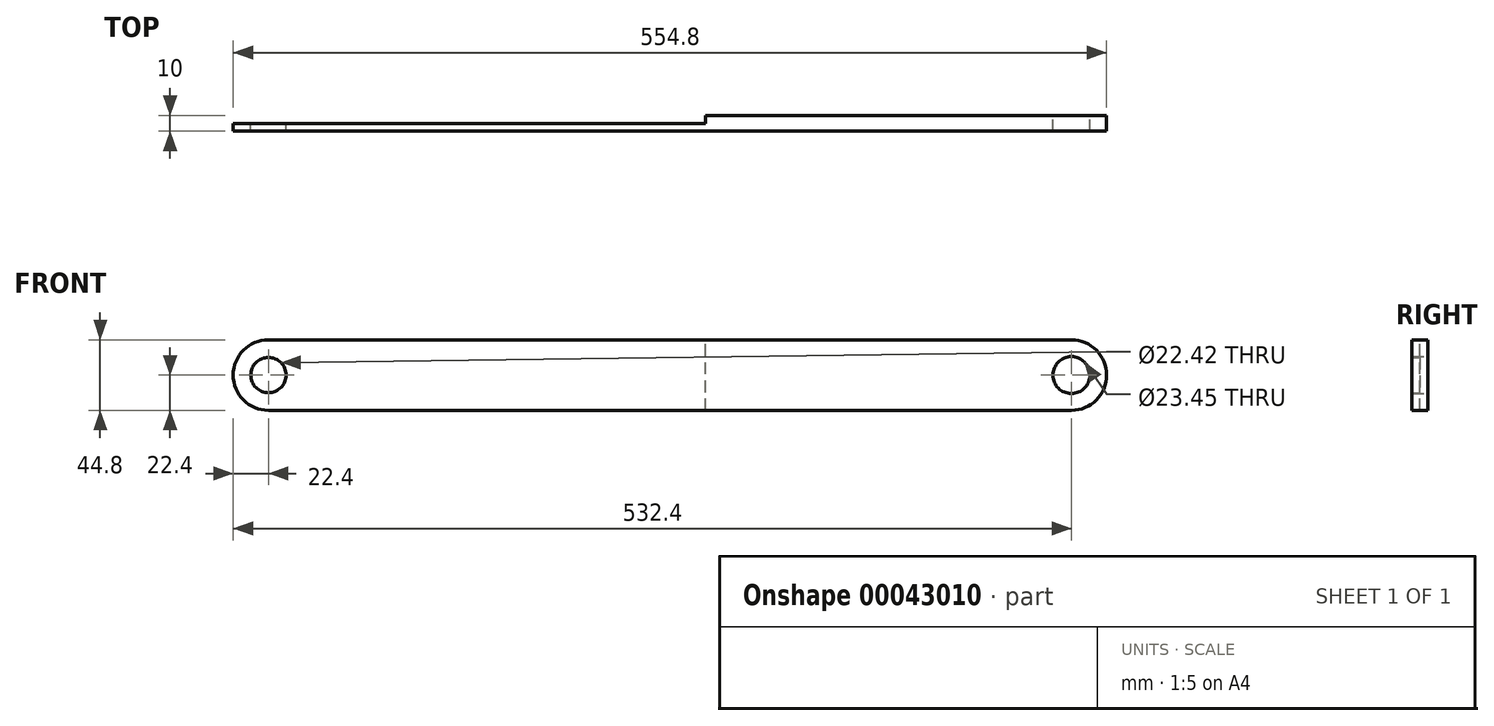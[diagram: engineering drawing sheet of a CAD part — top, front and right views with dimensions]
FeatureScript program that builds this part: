
annotation { "Feature Type Name" : "Feature", "Feature Type Description" : "" }
export const myFeature = defineFeature(function(context is Context, id is Id, definition is map)
    precondition{}
    {
        {
            var Q0;
            Q0=qCreatedBy(makeId("Front.planeOp"),FACE);
            var sketch = newSketch(context, id + "F0", { "sketchPlane" : qUnion([Q0])});
            skLineSegment(sketch, "E0.rect.bottom", {"start": v(255, 22.4) * mm, "end": v(-255, 22.4) * mm});
            skLineSegment(sketch, "E0.rect.top", {"start": v(255, -22.4) * mm, "end": v(-255, -22.4) * mm});
            skLineSegment(sketch, "E0.rect.left", {"start": v(255, 22.4) * mm, "end": v(255, -22.4) * mm, "construction": true});
            skLineSegment(sketch, "E0.rect.right", {"start": v(-255, 22.4) * mm, "end": v(-255, -22.4) * mm, "construction": true});
            skPoint(sketch, "E0.rect.middle", {"position": v(0, 0) * mm});
            skArc(sketch, "E1", {"start": v(-255, -22.4) * mm, "mid": v(-277.4, 0) * mm, "end": v(-255, 22.4) * mm});
            skArc(sketch, "E2", {"start": v(255, 22.4) * mm, "mid": v(277.4, 0) * mm, "end": v(255, -22.4) * mm});
            skCircle(sketch, "E3", {"center": v(-255, 0) * mm, "radius": 11.21 * mm});
            skCircle(sketch, "E4", {"center": v(255, 0) * mm, "radius": 11.73 * mm});
            skSolve(sketch);
        }
        {
            var Q0;
            Q0 = qSketchRegion(id + "F0", true);
            extrude(context, id + "F1", {"entities" : qUnion([Q0]), "depth" : 10 * mm});
        }
        {
            var Q0;
            Q0=makeQuery(id+"F1.opExtrude","SWEPT_FACE",FACE,{"disambiguationData":[OSD([sQuery(id+"F0.wireOp",EDGE,"E0.rect.bottom")])]});
            var sketch = newSketch(context, id + "F2", { "sketchPlane" : qUnion([Q0])});
            skLineSegment(sketch, "E5.rect.bottom", {"start": v(22.6, -5) * mm, "end": v(-277.4, -5) * mm});
            skLineSegment(sketch, "E5.rect.top", {"start": v(22.12, 10.83) * mm, "end": v(-277.4, 10.83) * mm});
            skLineSegment(sketch, "E5.rect.right", {"start": v(22.6, -5) * mm, "end": v(22.12, 10.83) * mm});
            skPoint(sketch, "E5.rect.middle", {"position": v(-127.64, 2.92) * mm});
            skLineSegment(sketch, "E6.0.0", {"start": v(-255, 0) * mm, "end": v(-277.4, 0) * mm});
            skLineSegment(sketch, "E6.0.1", {"start": v(-255, 0) * mm, "end": v(-255, -10) * mm});
            skLineSegment(sketch, "E6.0.2", {"start": v(-277.4, -10) * mm, "end": v(-255, -10) * mm});
            skLineSegment(sketch, "E6.0.3", {"start": v(-255, -10) * mm, "end": v(-255, 0) * mm});
            skLineSegment(sketch, "E7", {"start": v(-277.4, -10) * mm, "end": v(-277.4, 0) * mm, "construction": true});
            skLineSegment(sketch, "E8", {"start": v(-277.4, -5) * mm, "end": v(-277.4, 10.83) * mm});
            skSolve(sketch);
        }
        {
            var Q0;
            {var subQ0=sQuery(id+"F2.wireOp",EDGE,"E5.rect.right");var subQ4=sQuery(id+"F2.wireOp",EDGE,"E5.rect.top");var subQ5=makeQuery(id+"F2.imprint","INTERSECT",VERTEX,{"derivedFrom":[subQ4,subQ0]});Q0=makeQuery(id+"F2.imprint","IMPRINT",FACE,{"disambiguationData":[TD([[makeQuery(id+"F2.imprint","IMPRINT",EDGE,{"disambiguationData":[TD([[subQ5,1.0]])],"derivedFrom":subQ0}),1.0]])]});}
            var Q1;
            {var subQ6=sQuery(id+"F2.wireOp",EDGE,"E5.rect.bottom");Q1=makeQuery(id+"F2.imprint","IMPRINT",FACE,{"disambiguationData":[TD([[makeQuery(id+"F2.imprint","IMPRINT",EDGE,{"derivedFrom":subQ6}),-1.0]])]});}
            var Q2;
            Q2=sQuery(id+"F2.wireOp",EDGE,"b1f31f8f-e980-4ffb-8500-015411da009f");
            extrude(context, id + "F3", {"entities" : qUnion([Q0, Q1]), "operationType" : NewBodyOperationType.REMOVE, "surfaceEntities" : qUnion([Q2]), "oppositeDirection" : true, "depth" : 150 * mm});
        }
    });
